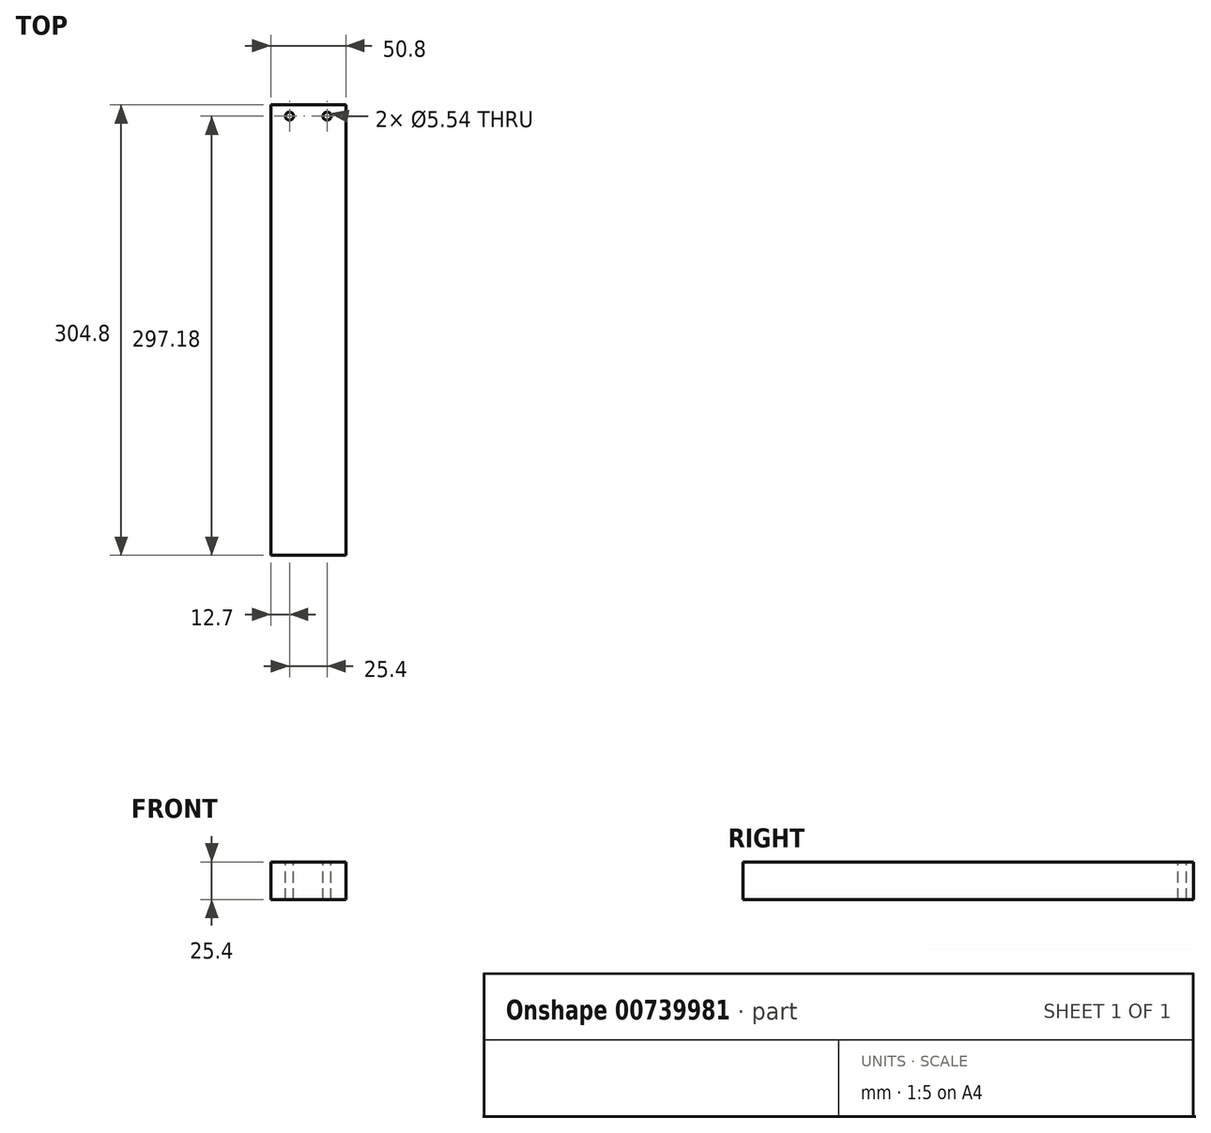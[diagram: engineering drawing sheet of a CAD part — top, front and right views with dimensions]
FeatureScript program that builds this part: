
annotation { "Feature Type Name" : "Feature", "Feature Type Description" : "" }
export const myFeature = defineFeature(function(context is Context, id is Id, definition is map)
    precondition{}
    {
        {
            var Q0;
            Q0=qCreatedBy(makeId("Front.planeOp"),FACE);
            var sketch = newSketch(context, id + "F0", { "sketchPlane" : qUnion([Q0])});
            skLineSegment(sketch, "E0.bottom", {"start": v(0, 0) * mm, "end": v(50.8, 0) * mm});
            skLineSegment(sketch, "E0.top", {"start": v(0, 25.4) * mm, "end": v(50.8, 25.4) * mm});
            skLineSegment(sketch, "E0.left", {"start": v(0, 0) * mm, "end": v(0, 25.4) * mm});
            skLineSegment(sketch, "E0.right", {"start": v(50.8, 0) * mm, "end": v(50.8, 25.4) * mm});
            skSolve(sketch);
        }
        {
            var Q0;
            Q0 = qSketchRegion(id + "F0", true);
            extrude(context, id + "F1", {"entities" : qUnion([Q0]), "depth" : 304.8 * mm, "offsetDistance" : 25.4 * mm});
        }
        {
            var Q0;
            Q0=makeQuery(id+"F1.opExtrude","SWEPT_FACE",FACE,{"disambiguationData":[OSD([sQuery(id+"F0.wireOp",EDGE,"E0.top")])]});
            var sketch = newSketch(context, id + "F2", { "sketchPlane" : qUnion([Q0])});
            skCircle(sketch, "E1", {"center": v(38.1, -7.62) * mm, "radius": 2.77 * mm});
            skCircle(sketch, "E2", {"center": v(12.7, -7.62) * mm, "radius": 2.77 * mm});
            skSolve(sketch);
        }
        {
            var Q0;
            Q0 = qSketchRegion(id + "F2", true);
            extrude(context, id + "F3", {"entities" : qUnion([Q0]), "operationType" : NewBodyOperationType.REMOVE, "endBound" : BoundingType.THROUGH_ALL, "oppositeDirection" : true, "depth" : 25.4 * mm, "offsetDistance" : 25.4 * mm});
        }
    });
